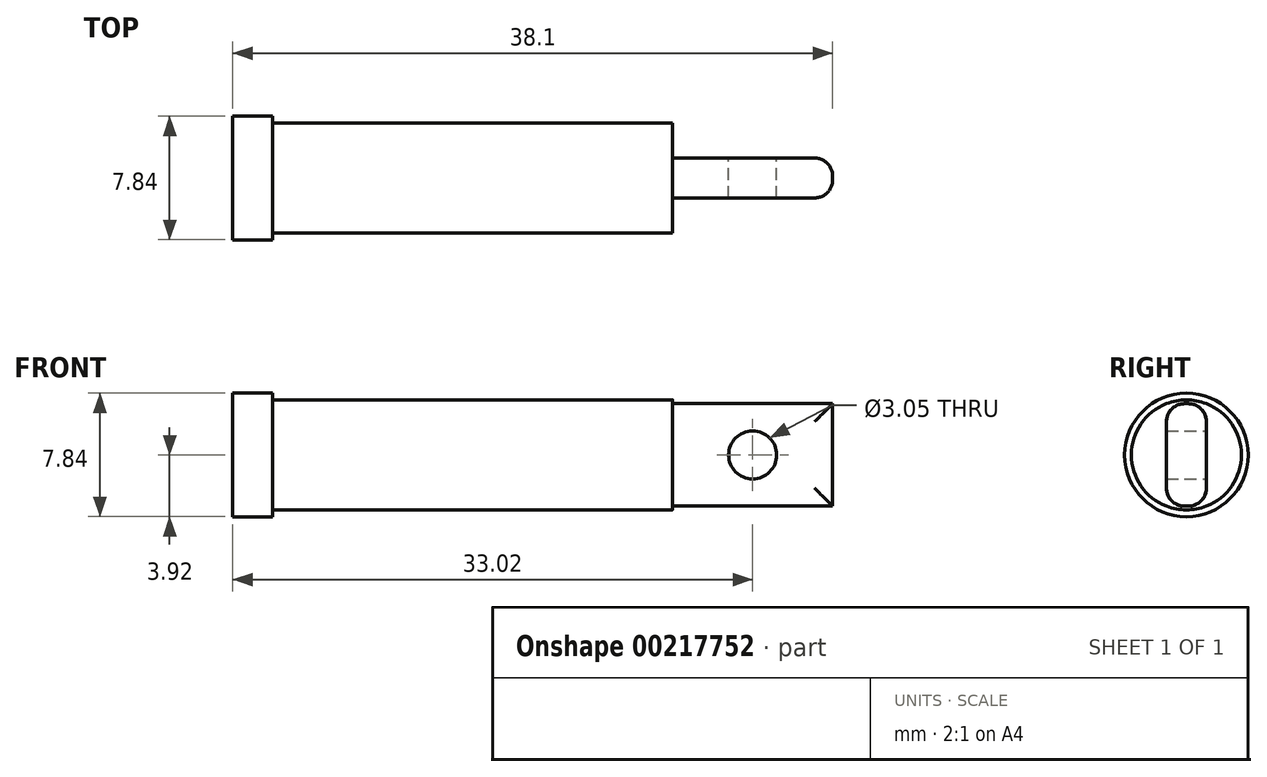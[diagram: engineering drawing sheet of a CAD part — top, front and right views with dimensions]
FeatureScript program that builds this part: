
annotation { "Feature Type Name" : "Feature", "Feature Type Description" : "" }
export const myFeature = defineFeature(function(context is Context, id is Id, definition is map)
    precondition{}
    {
        {
            var Q0;
            Q0=qCreatedBy(makeId("Right.planeOp"),FACE);
            var sketch = newSketch(context, id + "F0", { "sketchPlane" : qUnion([Q0])});
            skCircle(sketch, "E0", {"center": v(0, 0) * mm, "radius": 3.92 * mm});
            skSolve(sketch);
        }
        {
            var Q0;
            Q0 = qSketchRegion(id + "F0", true);
            extrude(context, id + "F1", {"entities" : qUnion([Q0]), "depth" : 2.54 * mm});
        }
        {
            var Q0;
            Q0=makeQuery(id+"F1.opExtrude","CAP_FACE",FACE,{"disambiguationData":[OSD([sQuery(id+"F0.wireOp",EDGE,"E0")])],"isStart":false});
            var sketch = newSketch(context, id + "F2", { "sketchPlane" : qUnion([Q0])});
            skCircle(sketch, "E1", {"center": v(0, 0) * mm, "radius": 3.5 * mm});
            skSolve(sketch);
        }
        {
            var Q0;
            Q0 = qSketchRegion(id + "F2", true);
            extrude(context, id + "F3", {"entities" : qUnion([Q0]), "operationType" : NewBodyOperationType.ADD, "depth" : 25.4 * mm});
        }
        {
            var Q0;
            Q0=makeQuery(id+"F3.opExtrude","CAP_FACE",FACE,{"disambiguationData":[OSD([sQuery(id+"F2.wireOp",EDGE,"E1")])],"isStart":false});
            var sketch = newSketch(context, id + "F4", { "sketchPlane" : qUnion([Q0])});
            skLineSegment(sketch, "E2.bottom", {"start": v(1.27, -3.25) * mm, "end": v(-1.27, -3.25) * mm});
            skLineSegment(sketch, "E2.top", {"start": v(1.27, 3.25) * mm, "end": v(-1.27, 3.25) * mm});
            skLineSegment(sketch, "E2.left", {"start": v(1.27, -3.25) * mm, "end": v(1.27, 3.25) * mm});
            skLineSegment(sketch, "E2.right", {"start": v(-1.27, -3.25) * mm, "end": v(-1.27, 3.25) * mm});
            skPoint(sketch, "E2.middle", {"position": v(0, 0) * mm});
            skSolve(sketch);
        }
        {
            var Q0;
            Q0 = qSketchRegion(id + "F4", true);
            extrude(context, id + "F5", {"entities" : qUnion([Q0]), "operationType" : NewBodyOperationType.ADD, "depth" : 10.16 * mm});
        }
        {
            var Q0;
            Q0=makeQuery(id+"F5.opExtrude","SWEPT_FACE",FACE,{"disambiguationData":[OSD([sQuery(id+"F4.wireOp",EDGE,"E2.left")])]});
            var sketch = newSketch(context, id + "F6", { "sketchPlane" : qUnion([Q0])});
            skCircle(sketch, "E3", {"center": v(-33.02, 0) * mm, "radius": 1.52 * mm});
            skSolve(sketch);
        }
        {
            var Q0;
            Q0 = qSketchRegion(id + "F6", true);
            extrude(context, id + "F7", {"entities" : qUnion([Q0]), "operationType" : NewBodyOperationType.REMOVE, "oppositeDirection" : true, "depth" : 25.4 * mm});
        }
        {
            var Q0;
            Q0=makeQuery(id+"F5.opExtrude","CAP_EDGE",EDGE,{"disambiguationData":[OSD([sQuery(id+"F4.wireOp",EDGE,"E2.left")])],"isStart":false});
            var Q1;
            Q1=makeQuery(id+"F5.opExtrude","CAP_EDGE",EDGE,{"disambiguationData":[OSD([sQuery(id+"F4.wireOp",EDGE,"E2.right")])],"isStart":false});
            var Q2;
            Q2=makeQuery(id+"F5.opExtrude","SWEPT_EDGE",EDGE,{"disambiguationData":[OSD([sQuery(id+"F2.wireOp",EDGE,"E1"),sQuery(id+"F4.wireOp",EDGE,"E2.top"),sQuery(id+"F4.wireOp",EDGE,"E2.left")])]});
            var Q3;
            Q3=makeQuery(id+"F5.opExtrude","SWEPT_EDGE",EDGE,{"disambiguationData":[OSD([sQuery(id+"F2.wireOp",EDGE,"E1"),sQuery(id+"F4.wireOp",EDGE,"E2.top"),sQuery(id+"F4.wireOp",EDGE,"E2.right")])]});
            var Q4;
            Q4=makeQuery(id+"F5.opExtrude","SWEPT_EDGE",EDGE,{"disambiguationData":[OSD([sQuery(id+"F2.wireOp",EDGE,"E1"),sQuery(id+"F4.wireOp",EDGE,"E2.bottom"),sQuery(id+"F4.wireOp",EDGE,"E2.left")])]});
            var Q5;
            Q5=makeQuery(id+"F5.opExtrude","SWEPT_EDGE",EDGE,{"disambiguationData":[OSD([sQuery(id+"F2.wireOp",EDGE,"E1"),sQuery(id+"F4.wireOp",EDGE,"E2.bottom"),sQuery(id+"F4.wireOp",EDGE,"E2.right")])]});
            fillet(context, id + "F8", {"entities" : qUnion([Q0, Q1, Q2, Q3, Q4, Q5]), "radius" : 1.14 * mm, "tangentPropagation" : true, "allowEdgeOverflow" : false});
        }
    });
